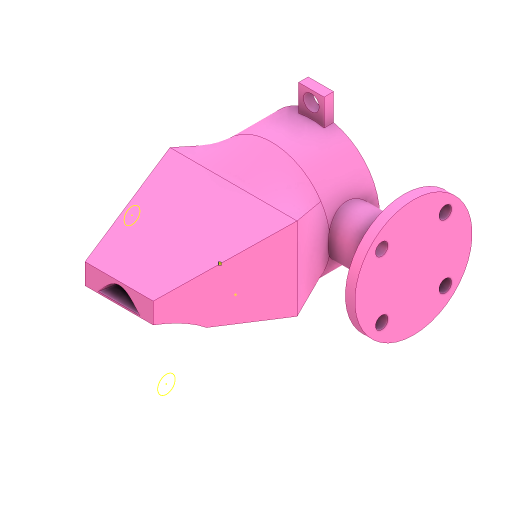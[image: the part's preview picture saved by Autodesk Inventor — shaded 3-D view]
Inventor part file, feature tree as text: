
AUTODESK INVENTOR PART (.ipt)
format: ipt  version: 2024 (Build 280153000, 153)  size: 1,533,952 bytes
history: native  units: mm
features: sketch x25, extrude x22, projected_geometry x11, split x10, other x10, boolean_combine x6, loft x5, plane x4, fillet x2, sweep x2, thicken_offset x2
ambient origin geometry x8: Origin, YZ Plane, XZ Plane, XY Plane, X Axis, Y Axis, Z Axis, Center Point
bodies: Solid1 (feature_tree), Solid2 (feature_tree), Solid19 (feature_tree), Solid21 (feature_tree), Solid22 (feature_tree), Solid23 (feature_tree), Solid3 (feature_tree), Solid4 (feature_tree), Solid5 (feature_tree), Solid6 (feature_tree), Solid7 (feature_tree), Solid8 (feature_tree), Solid9 (feature_tree), Solid10 (feature_tree), Solid11 (feature_tree), Solid12 (feature_tree), Solid13 (feature_tree), Solid14 (feature_tree), Solid15 (feature_tree), Solid16 (feature_tree), Solid17 (feature_tree), Solid18 (feature_tree)
feature tree (99):
  extrude  "Extrusion1"  Depth=9.5mm TaperAngle=0.0deg
  extrude  "Extrusion2"  Depth=3.0mm TaperAngle=0.0deg
  extrude  "Extrusion3"  Depth=40.0mm
  plane  "Work Plane2"
  sketch  "Sketch4"  dims[d4=29.0mm d5=3.0mm d6=0.0mm]
  loft  "Loft1"
  loft  "Loft2"
  loft  "Loft3"
  loft  "Loft4"
  boolean_combine  "Combine1"
  loft  "Loft5"
  fillet  "Fillet1"  [1 undecoded]
  fillet  "Fillet2"  [1 undecoded]
  plane  "Work Plane3"
  extrude  "Extrusion5"  TaperAngle=0.0deg  [1 undecoded]
  extrude  "Extrusion6"  TaperAngle=0.0deg  [1 undecoded]
  extrude  "Extrusion7"  Depth=40.0mm
  extrude  "Extrusion8"  TaperAngle=0.0deg  [1 undecoded]
  extrude  "Extrusion9"  Depth=2.0mm
  extrude  "Extrusion10"  Depth=38.0mm
  extrude  "Extrusion11"  Depth=3.0mm TaperAngle=0.0deg
  extrude  "Extrusion12"  Depth=3.0mm TaperAngle=0.0deg
  extrude  "Extrusion14"  Depth=12.5mm TaperAngle=0.0deg
  extrude  "Extrusion15"  Depth=3.7mm TaperAngle=0.0deg
  split  "Split1"
  split  "Split2"
  split  "Split3"
  split  "Split4"
  split  "Split5"
  split  "Split6"
  split  "Split7"
  boolean_combine  "Combine2"
  split  "Split8"
  boolean_combine  "Combine3"
  boolean_combine  "Combine4"
  extrude  "Extrusion16"  Depth=8.5mm
  extrude  "Extrusion17"  Depth=8.5mm
  sketch  "Sketch36"  dims[d43=1.5mm d46=38.0mm]
  sweep  "Sweep1"
  split  "Split9"
  thicken_offset  "Thicken1"
  extrude  "Extrusion18"  Depth=10.0mm
  sweep  "Sweep2"
  split  "Split10"
  thicken_offset  "Thicken2"
  boolean_combine  "Combine5"
  plane  "Work Plane4"
  extrude  "Extrusion19"  Depth=2.5mm TaperAngle=0.0deg
  other  "Work Point1"
  other  "Work Point2"
  other  "Work Point3"
  extrude  "Extrusion20"  Depth=5.5mm
  extrude  "Extrusion21"  Depth=8.5mm
  extrude  "Extrusion22"  Depth=8.5mm
  extrude  "Extrusion23"  Depth=2.5mm TaperAngle=0.0deg
  extrude  "Extrusion24"  Depth=2.5mm TaperAngle=0.0deg
  boolean_combine  "Combine6"
  sketch  "Sketch1"  dims[d0=3.0mm d1=0.0mm d2=9.5mm d3=0.0mm]
  plane  "Work Plane1"
  other  "2D Equation Curve1"
  other  "Edges1"
  other  "Edges2"
  other  "Edges3"
  other  "Edges4"
  sketch  "Sketch7"  dims[d7=12.0mm d8=36.0mm d9=40.0mm]
  sketch  "Sketch10"  dims[d10=9.0mm d11=10.0mm]
  sketch  "Sketch12"  dims[d12=3.0mm d13=-6.5mm d14=6.5mm]
  sketch  "Sketch13"  dims[d15=40.0mm d16=26.0mm]
  sketch  "Sketch16"  dims[d17=20.0mm d18=20.0mm]
  projected_geometry  "Projected Loop1"
  sketch  "Sketch19"  dims[d19=0.0mm d20=90.0deg d21=0.0mm d22=90.0deg d23=0.0mm d24=90.0deg d25=0.0mm d26=90.0deg]
  projected_geometry  "Projected Loop2"
  projected_geometry  "Projected Loop3"
  projected_geometry  "Projected Loop4"
  projected_geometry  "Projected Loop5"
  sketch  "Sketch23"  dims[d27=0.0mm d28=90.0deg d29=0.0mm d30=90.0deg]
  sketch  "Sketch24"  dims[d31=0.0mm d32=90.0deg d33=0.0mm d34=90.0deg]
  sketch  "Sketch28"  dims[d35=26.0mm d36=40.0mm]
  sketch  "Sketch29"  dims[d37=4.0mm d38=0.0mm d39=90.0deg]
  sketch  "Sketch35"  dims[d40=0.0mm d41=90.0deg d42=2.0mm]
  projected_geometry  "Projected Loop11"
  sketch  "3D Sketch2"
  other  "Srf1"
  sketch  "Sketch38"  dims[d47=15.0mm d48=3.0mm d49=0.0mm]
  projected_geometry  "Projected Loop12"
  sketch  "Sketch46"  dims[d50=15.0mm d51=3.0mm d52=0.0mm]
  projected_geometry  "Projected Loop21"
  sketch  "3D Sketch3"
  sketch  "Sketch47"  dims[d53=11.0mm d54=12.5mm d55=0.0mm]
  projected_geometry  "Projected Loop22"
  sketch  "Sketch49"  dims[d56=11.0mm d57=3.7mm d58=0.0mm]
  sketch  "Sketch50"  dims[d59=20.0mm d60=0.0mm d61=8.5mm]
  sketch  "Sketch52"  dims[d62=8.5mm d63=8.5mm]
  sketch  "Sketch53"  dims[d64=8.5mm d65=2.7mm d66=0.0mm]
  projected_geometry  "Projected Loop25"
  projected_geometry  "Projected Loop26"
  sketch  "Sketch54"  dims[d67=40.0mm d68=10.0mm]
  sketch  "Sketch56"  dims[d69=2.7mm d70=0.0mm d71=2.5mm d72=0.0mm d73=2.5mm d74=0.0mm d80=5.5mm d81=8.5mm d82=8.5mm d83=2.5mm d84=0.0mm d85=2.5mm d86=0.0mm d87=0.5mm d88=0.0mm d89=0.0mm d91=10.0mm d92=10.0mm d93=0.1mm d94=0.0mm d95=16.5mm d96=2.5mm d97=4.0mm d98=2.5mm d99=2.5mm d100=5.0mm d101=5.0mm d102=2.5mm d103=2.5mm d104=2.5mm d105=2.5mm d106=0.0mm d107=0.0mm d108=2.5mm d109=2.5mm d114=0.1mm d115=0.1mm d116=0.1mm d117=0.0mm d118=15.0mm d119=3.0mm d120=1.6mm d121=1.5mm d122=16.5mm d125=5.5mm d126=2.5mm d127=2.5mm d128=0.0mm d129=0.0mm d130=0.1mm d131=0.1mm d132=58.25mm d133=6.0mm d134=16.0mm d135=0.0mm d136=12.0mm d137=12.0mm d138=12.0mm d139=12.0mm d140=10.0mm d141=0.0mm d142=0.0mm d143=0.0mm d144=0.0mm d145=0.0mm d146=0.0mm d147=0.0mm d148=9.273806mm d149=9.273806mm d150=0.0mm d151=0.0mm d110=0.5mm d111=0.872665mm d112=0.5mm d113=0.872665mm]
  other  "Unwrap1"
note: 5 required parameter values undecoded (feature->parameter linkage not recoverable at this tier; creation-order binding heuristic only, values carry confidence <= 0.55)
